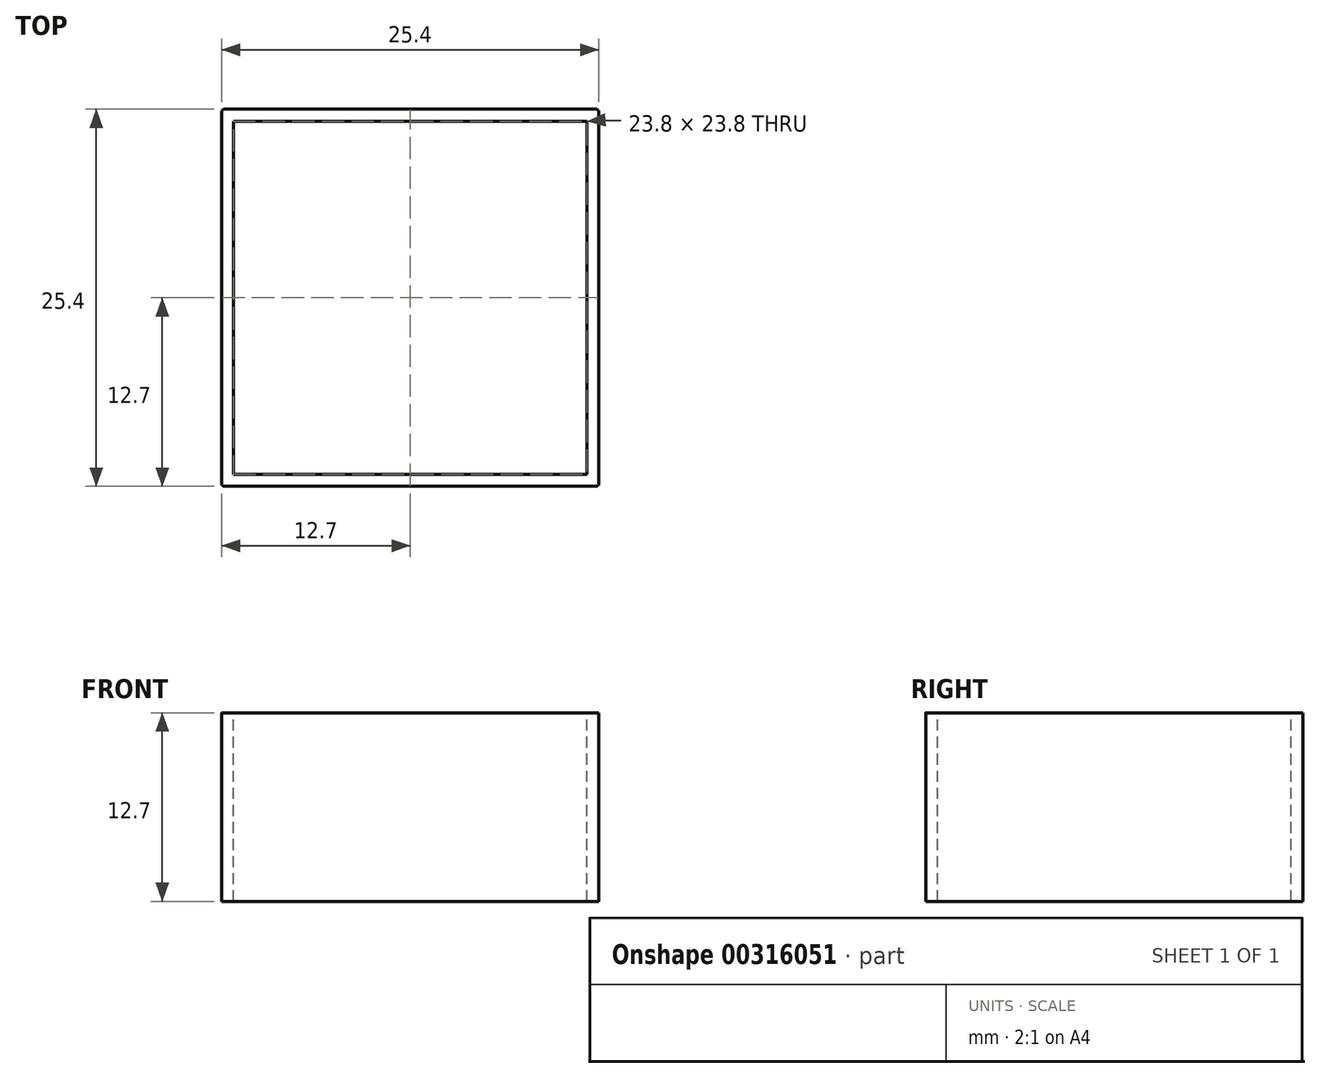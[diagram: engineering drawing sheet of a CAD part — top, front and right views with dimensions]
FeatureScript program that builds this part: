
annotation { "Feature Type Name" : "Feature", "Feature Type Description" : "" }
export const myFeature = defineFeature(function(context is Context, id is Id, definition is map)
    precondition{}
    {
        {
            var Q0;
            Q0=qCreatedBy(makeId("Top.planeOp"),FACE);
            var sketch = newSketch(context, id + "F0", { "sketchPlane" : qUnion([Q0])});
            skLineSegment(sketch, "E0.bottom", {"start": v(12.7, -12.7) * mm, "end": v(-12.7, -12.7) * mm});
            skLineSegment(sketch, "E0.top", {"start": v(12.7, 12.7) * mm, "end": v(-12.7, 12.7) * mm});
            skLineSegment(sketch, "E0.left", {"start": v(12.7, -12.7) * mm, "end": v(12.7, 12.7) * mm});
            skLineSegment(sketch, "E0.right", {"start": v(-12.7, -12.7) * mm, "end": v(-12.7, 12.7) * mm});
            skPoint(sketch, "E0.middle", {"position": v(0, 0) * mm});
            skSolve(sketch);
        }
        {
            var Q0;
            Q0 = qSketchRegion(id + "F0", true);
            extrude(context, id + "F1", {"entities" : qUnion([Q0]), "depth" : 12.7 * mm});
        }
        {
            var Q0;
            Q0=makeQuery(id+"F1.opExtrude","SWEPT_EDGE",EDGE,{"disambiguationData":[OSD([sQuery(id+"F0.wireOp",EDGE,"E0.bottom"),sQuery(id+"F0.wireOp",EDGE,"E0.left")])]});
            var Q1;
            Q1=makeQuery(id+"F1.opExtrude","SWEPT_EDGE",EDGE,{"disambiguationData":[OSD([sQuery(id+"F0.wireOp",EDGE,"E0.top"),sQuery(id+"F0.wireOp",EDGE,"E0.left")])]});
            var Q2;
            Q2=makeQuery(id+"F1.opExtrude","SWEPT_EDGE",EDGE,{"disambiguationData":[OSD([sQuery(id+"F0.wireOp",EDGE,"E0.bottom"),sQuery(id+"F0.wireOp",EDGE,"E0.right")])]});
            var Q3;
            Q3=makeQuery(id+"F1.opExtrude","SWEPT_EDGE",EDGE,{"disambiguationData":[OSD([sQuery(id+"F0.wireOp",EDGE,"E0.top"),sQuery(id+"F0.wireOp",EDGE,"E0.right")])]});
            fillet(context, id + "F2", {"entities" : qUnion([Q0, Q1, Q2, Q3]), "radius" : .2 * mm, "tangentPropagation" : true, "allowEdgeOverflow" : false});
        }
        {
            var Q0;
            Q0=makeQuery(id+"F1.opExtrude","CAP_FACE",FACE,{"disambiguationData":[OSD([sQuery(id+"F0.wireOp",EDGE,"E0.bottom"),sQuery(id+"F0.wireOp",EDGE,"E0.top"),sQuery(id+"F0.wireOp",EDGE,"E0.left"),sQuery(id+"F0.wireOp",EDGE,"E0.right")])],"isStart":false});
            var Q1;
            Q1=makeQuery(id+"F1.opExtrude","CAP_FACE",FACE,{"disambiguationData":[OSD([sQuery(id+"F0.wireOp",EDGE,"E0.bottom"),sQuery(id+"F0.wireOp",EDGE,"E0.top"),sQuery(id+"F0.wireOp",EDGE,"E0.left"),sQuery(id+"F0.wireOp",EDGE,"E0.right")])],"isStart":true});
            shell(context, id + "F3", {"entities" : qUnion([Q0, Q1]), "thickness" : .8 * mm});
        }
    });
